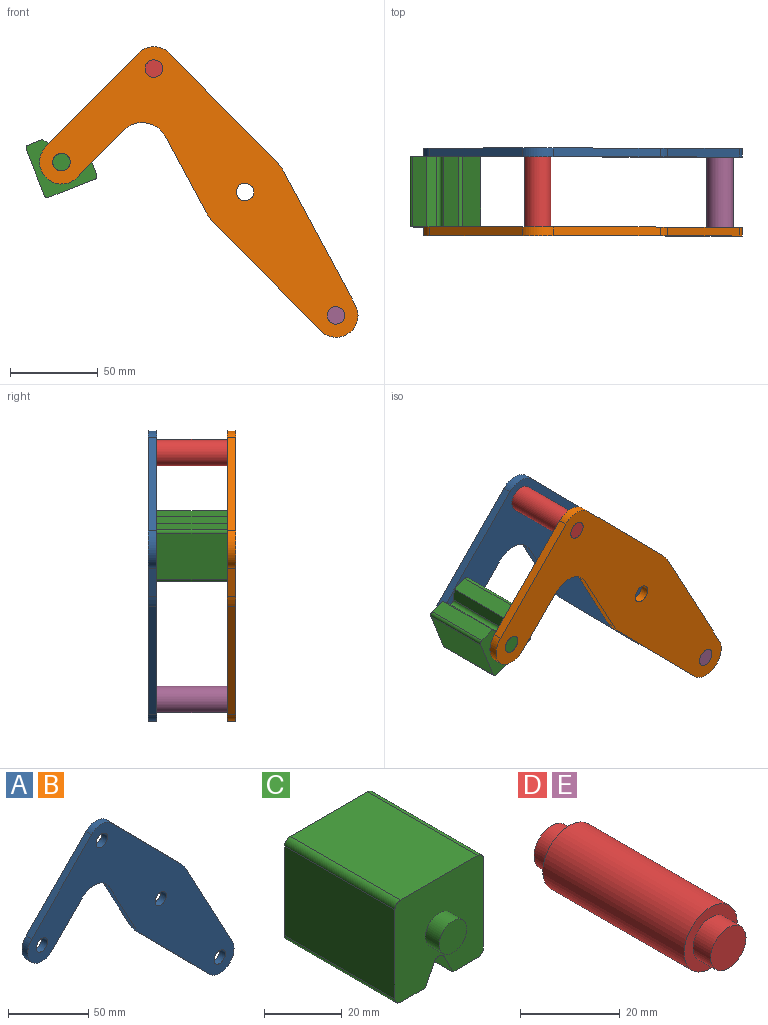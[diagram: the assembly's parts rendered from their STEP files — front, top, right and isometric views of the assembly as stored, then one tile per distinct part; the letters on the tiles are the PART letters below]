
ASSEMBLY  parts=5 mates=3
PART A: 18 faces, bbox 181.7x5x165.8 mm
  f0: plane 43.49x23.35mm, normal (-0.88,0,-0.47), area 246.8mm2, adj f1,f14,f16,f17
  f1: cylinder r=25mm len=5.75mm, axis (0,1,0), area 35.8mm2, adj f0,f2,f16,f17
  f2: plane 61.6x60.87mm, normal (-0.71,0,-0.7), area 433mm2, adj f1,f3,f16,f17
  f3: cylinder r=12.5mm len=21.39mm, axis (0,1,0), area 178.4mm2, adj f2,f4,f16,f17
  f4: plane 76.3x40.96mm, normal (0.88,0,0.47), area 433mm2, adj f3,f5,f16,f17
  f5: cylinder r=25mm len=5.75mm, axis (0,1,0), area 35.8mm2, adj f4,f6,f16,f17
  f6: plane 61.6x60.87mm, normal (0.71,0,0.7), area 433mm2, adj f5,f7,f16,f17
  f7: cylinder r=12.5mm len=17.78mm, axis (0,1,0), area 98.9mm2, adj f6,f8,f16,f17
  f8: plane 53.35x52.71mm, normal (-0.71,0,0.7), area 375mm2, adj f7,f9,f16,f17
  f9: cylinder r=12.5mm len=21.39mm, axis (0,1,0), area 196.3mm2, adj f8,f10,f16,f17
  f10: plane 26.86x26.54mm, normal (0.71,0,-0.7), area 188.8mm2, adj f9,f14,f16,f17
  f11: cylinder r=5mm len=10mm, axis (0,1,0), area 157.1mm2, adj f16,f17
  f12: cylinder r=5mm len=10mm, axis (0,1,0), area 157.1mm2, adj f16,f17
  f13: cylinder r=5mm len=10mm, axis (0,1,0), area 157.1mm2, adj f16,f17
  f14: cylinder r=15mm len=23.89mm, axis (0,1,0), area 140.2mm2, adj f0,f10,f16,f17
  f15: cylinder r=5mm len=10mm, axis (0,1,0), area 157.1mm2, adj f16,f17
  f16: plane 181.66x165.78mm, normal (0,-1,0), area 8710.1mm2, adj f0,f1,f2,f3,f4,f5,f6,f7
  f17: plane 181.66x165.78mm, normal (0,1,0), area 8710.1mm2, adj f0,f1,f2,f3,f4,f5,f6,f7
PART B: same geometry as A
PART C: 18 faces, bbox 32.1x50x32.1 mm
  f0: plane 40x28.08mm, normal (1,0,0), area 1123.1mm2, adj f4,f10,f13,f14
  f1: plane 40x9.04mm, normal (0,0,-1), area 361.6mm2, adj f2,f4,f10,f14
  f2: plane 40x6.42mm, normal (-0.89,0,-0.45), area 287.2mm2, adj f1,f4,f10,f15
  f3: plane 40x6.42mm, normal (0.89,0,-0.45), area 287.2mm2, adj f4,f5,f10,f15
  f4: plane 32.08x32.08mm, normal (0,-1,0), area 900.6mm2, adj f0,f1,f2,f3,f5,f6,f7,f9
  f5: plane 40x9.04mm, normal (0,0,-1), area 361.6mm2, adj f3,f4,f10,f16
  f6: plane 40x28.08mm, normal (0,0,1), area 1123.1mm2, adj f4,f10,f13,f17
  f7: plane 40x28.08mm, normal (-1,0,0), area 1123.1mm2, adj f4,f10,f16,f17
  f8: plane 10x10mm, normal (0,-1,0), area 78.5mm2, adj f9
  f9: cylinder r=5mm len=10mm, axis (0,1,0), area 157.1mm2, adj f4,f8
  f10: plane 32.08x32.08mm, normal (0,1,0), area 900.6mm2, adj f0,f1,f2,f3,f5,f6,f7,f12
  f11: plane 10x10mm, normal (0,1,0), area 78.5mm2, adj f12
  f12: cylinder r=5mm len=10mm, axis (0,-1,0), area 157.1mm2, adj f10,f11
  f13: cylinder r=2mm len=40mm, axis (0,1,0), area 125.7mm2, adj f0,f4,f6,f10
  f14: cylinder r=2mm len=40mm, axis (0,-1,0), area 125.7mm2, adj f0,f1,f4,f10
  f15: cylinder r=2mm len=40mm, axis (0,1,0), area 177.1mm2, adj f2,f3,f4,f10
  f16: cylinder r=2mm len=40mm, axis (0,1,0), area 125.7mm2, adj f4,f5,f7,f10
  f17: cylinder r=2mm len=40mm, axis (0,-1,0), area 125.7mm2, adj f4,f6,f7,f10
PART D: 7 faces, bbox 15x50x15 mm
  f0: cylinder r=7.5mm len=40mm, axis (0,-1,0), area 1885mm2, adj f2,f5
  f1: cylinder r=5mm len=10mm, axis (0,1,0), area 157.1mm2, adj f2,f3
  f2: plane 15x15mm, normal (0,-1,0), area 98.2mm2, adj f0,f1
  f3: plane 10x10mm, normal (0,-1,0), area 78.5mm2, adj f1
  f4: cylinder r=5mm len=10mm, axis (0,-1,0), area 157.1mm2, adj f5,f6
  f5: plane 15x15mm, normal (0,1,0), area 98.2mm2, adj f0,f4
  f6: plane 10x10mm, normal (0,1,0), area 78.5mm2, adj f4
PART E: same geometry as D
PLACE A t=(0,25,0)mm
PLACE B t=(0,-20,0)mm fixed
PLACE C rot(axis=(0,1,0),158.5deg) t=(-208.32,-20,-5.54)mm
PLACE D t=(0,-20,0)mm
PLACE E t=(103.95,-20,-140.78)mm
MATE fastened A.f7 <-> D.f0  axis (0,1,0) through (-51.98,22.5,70.39)mm
MATE revolute C.f9 <-> B.f9  axis (0,1,0) through (-104.69,-22.5,17.04)mm
MATE fastened E.f0 <-> A.f3  axis (0,-1,0) through (51.98,22.5,-70.39)mm
